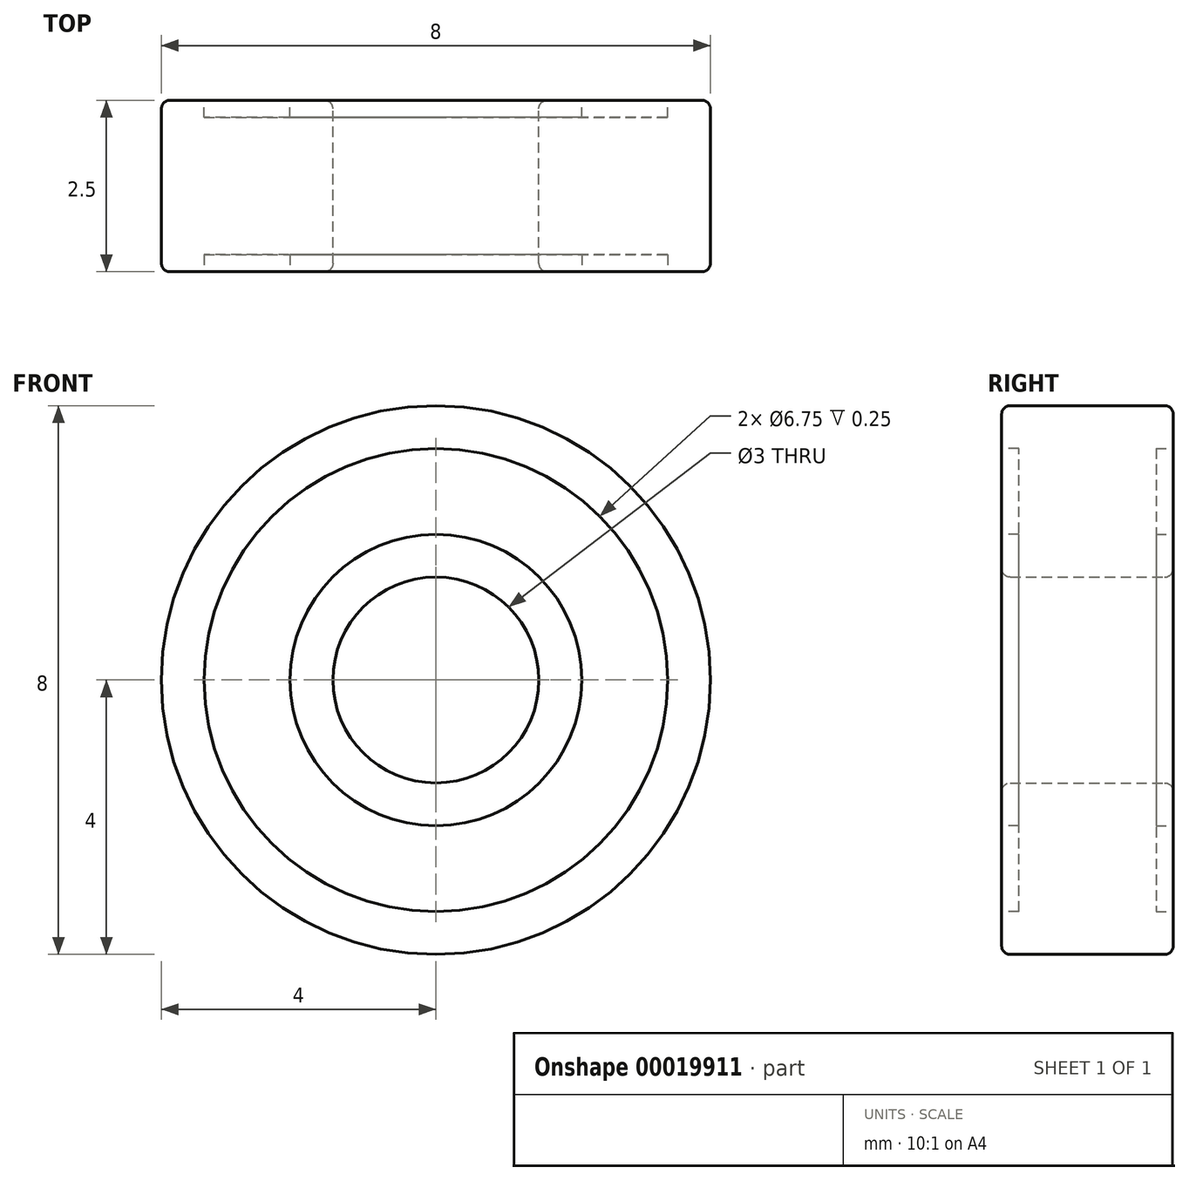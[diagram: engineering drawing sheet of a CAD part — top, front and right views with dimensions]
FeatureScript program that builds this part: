
annotation { "Feature Type Name" : "Feature", "Feature Type Description" : "" }
export const myFeature = defineFeature(function(context is Context, id is Id, definition is map)
    precondition{}
    {
        {
            var Q0;
            Q0=qCreatedBy(makeId("Front.planeOp"),FACE);
            var sketch = newSketch(context, id + "F0", { "sketchPlane" : qUnion([Q0])});
            skCircle(sketch, "E0", {"center": v(0, 0) * mm, "radius": 1.5 * mm});
            skCircle(sketch, "E1", {"center": v(0, 0) * mm, "radius": 4 * mm});
            skSolve(sketch);
        }
        {
            var Q0;
            Q0=qSketchRegion(id+"F0",true);
            extrude(context, id + "F1", {"entities" : qUnion([Q0]), "depth" : 1.25 * mm, "hasSecondDirection" : true, "secondDirectionOppositeDirection" : true, "secondDirectionDepth" : 1.25 * mm});
        }
        {
            var Q0;
            Q0=makeQuery(id+"F1.opExtrude","CAP_FACE",FACE,{"disambiguationData":[OSD([sQuery(id+"F0.wireOp",EDGE,"E0"),sQuery(id+"F0.wireOp",EDGE,"E1")])],"isStart":false});
            var sketch = newSketch(context, id + "F2", { "sketchPlane" : qUnion([Q0])});
            skCircle(sketch, "E2", {"center": v(0, 0) * mm, "radius": 2.12 * mm});
            skCircle(sketch, "E3", {"center": v(0, 0) * mm, "radius": 3.38 * mm});
            skSolve(sketch);
        }
        {
            var Q0;
            Q0=qSketchRegion(id+"F2",true);
            extrude(context, id + "F3", {"entities" : qUnion([Q0]), "operationType" : NewBodyOperationType.REMOVE, "oppositeDirection" : true, "depth" : .25 * mm});
        }
        {
            var Q0;
            Q0=makeQuery(id+"F1.opExtrude","CAP_FACE",FACE,{"disambiguationData":[OSD([sQuery(id+"F0.wireOp",EDGE,"E0"),sQuery(id+"F0.wireOp",EDGE,"E1")])],"isStart":true});
            var sketch = newSketch(context, id + "F4", { "sketchPlane" : qUnion([Q0])});
            skCircle(sketch, "E4", {"center": v(0, 0) * mm, "radius": 2.12 * mm});
            skCircle(sketch, "E5", {"center": v(0, 0) * mm, "radius": 3.38 * mm});
            skSolve(sketch);
        }
        {
            var Q0;
            Q0=qSketchRegion(id+"F4",true);
            extrude(context, id + "F5", {"entities" : qUnion([Q0]), "operationType" : NewBodyOperationType.REMOVE, "oppositeDirection" : true, "depth" : .25 * mm});
        }
        {
            var Q0;
            Q0=makeQuery(id+"F1.opExtrude","CAP_EDGE",EDGE,{"disambiguationData":[OSD([sQuery(id+"F0.wireOp",EDGE,"E1")])],"isStart":true});
            var Q1;
            Q1=makeQuery(id+"F1.opExtrude","CAP_EDGE",EDGE,{"disambiguationData":[OSD([sQuery(id+"F0.wireOp",EDGE,"E1")])],"isStart":false});
            var Q2;
            Q2=makeQuery(id+"F1.opExtrude","CAP_EDGE",EDGE,{"disambiguationData":[OSD([sQuery(id+"F0.wireOp",EDGE,"E0")])],"isStart":true});
            var Q3;
            Q3=makeQuery(id+"F1.opExtrude","CAP_EDGE",EDGE,{"disambiguationData":[OSD([sQuery(id+"F0.wireOp",EDGE,"E0")])],"isStart":false});
            fillet(context, id + "F6", {"entities" : qUnion([Q0, Q1, Q2, Q3]), "radius" : .125 * mm, "tangentPropagation" : true, "allowEdgeOverflow" : false});
        }
    });
